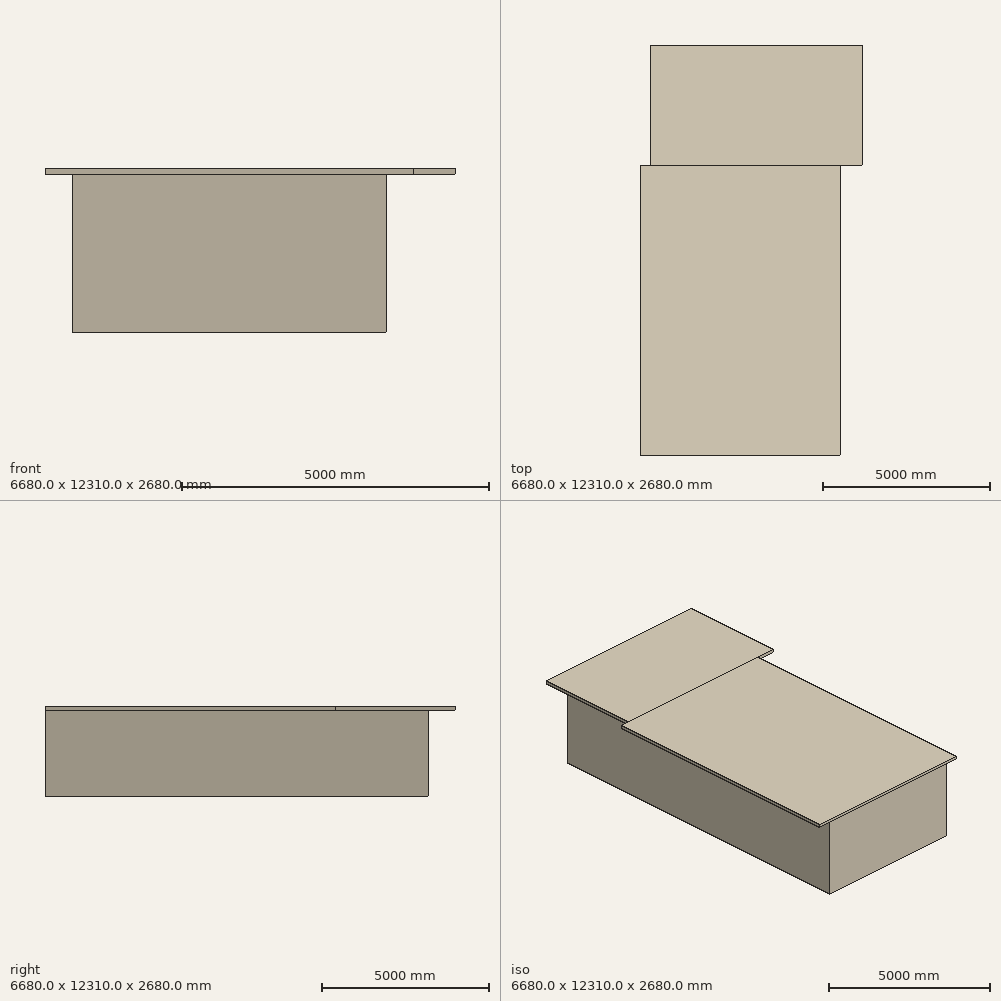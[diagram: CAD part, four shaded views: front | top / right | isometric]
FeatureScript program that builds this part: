
annotation { "Feature Type Name" : "Feature", "Feature Type Description" : "" }
export const myFeature = defineFeature(function(context is Context, id is Id, definition is map)
    precondition{}
    {
        {
            var Q0;
            Q0=qCreatedBy(makeId("Top.planeOp"),FACE);
            var sketch = newSketch(context, id + "F0", { "sketchPlane" : qUnion([Q0])});
            skLineSegment(sketch, "E0.bottom", {"start": v(0, 0) * mm, "end": v(5120, 0) * mm});
            skLineSegment(sketch, "E0.top", {"start": v(0, 11510) * mm, "end": v(5120, 11510) * mm});
            skLineSegment(sketch, "E0.left", {"start": v(0, 0) * mm, "end": v(0, 11510) * mm});
            skLineSegment(sketch, "E0.right", {"start": v(5120, 0) * mm, "end": v(5120, 11510) * mm});
            skLineSegment(sketch, "E1.bottom", {"start": v(5120, 11510) * mm, "end": v(0, 11510) * mm});
            skSolve(sketch);
        }
        {
            var Q0;
            Q0 = qSketchRegion(id + "F0", true);
            extrude(context, id + "F1", {"entities" : qUnion([Q0]), "depth" : 2580 * mm, "offsetDistance" : 25 * mm});
        }
        {
            var Q0;
            Q0=qCreatedBy(makeId("Front.planeOp"),FACE);
            var sketch = newSketch(context, id + "F2", { "sketchPlane" : qUnion([Q0])});
            skLineSegment(sketch, "E2.bottom", {"start": v(-440, 2580) * mm, "end": v(5560, 2580) * mm});
            skLineSegment(sketch, "E2.top", {"start": v(-440, 2680) * mm, "end": v(5560, 2680) * mm});
            skLineSegment(sketch, "E2.left", {"start": v(-440, 2580) * mm, "end": v(-440, 2680) * mm});
            skLineSegment(sketch, "E2.right", {"start": v(5560, 2580) * mm, "end": v(5560, 2680) * mm});
            skSolve(sketch);
        }
        {
            var Q0;
            Q0=makeQuery(id+"F2.imprint","IMPRINT",FACE,{"disambiguationData":[TD([[makeQuery(id+"F2.imprint","IMPRINT",EDGE,{"derivedFrom":sQuery(id+"F2.wireOp",EDGE,"E2.bottom")}),1.0]])]});
            extrude(context, id + "F3", {"entities" : qUnion([Q0]), "oppositeDirection" : true, "depth" : 8710 * mm, "offsetDistance" : 25 * mm});
        }
        {
            var Q0;
            Q0=makeQuery(id+"F3.opExtrude","SWEPT_FACE",FACE,{"disambiguationData":[OSD([sQuery(id+"F2.wireOp",EDGE,"E2.top")])]});
            var sketch = newSketch(context, id + "F4", { "sketchPlane" : qUnion([Q0])});
            skLineSegment(sketch, "E3.top", {"start": v(0, 8710) * mm, "end": v(5120, 8710) * mm});
            skLineSegment(sketch, "E4.bottom", {"start": v(6240, 8710) * mm, "end": v(-140, 8710) * mm});
            skLineSegment(sketch, "E4.top", {"start": v(6240, 12310) * mm, "end": v(-140, 12310) * mm});
            skLineSegment(sketch, "E4.left", {"start": v(6240, 8710) * mm, "end": v(6240, 12310) * mm});
            skLineSegment(sketch, "E4.right", {"start": v(-140, 8710) * mm, "end": v(-140, 12310) * mm});
            skSolve(sketch);
        }
        {
            var Q0;
            Q0 = qSketchRegion(id + "F4", true);
            extrude(context, id + "F5", {"entities" : qUnion([Q0]), "oppositeDirection" : true, "depth" : 100 * mm, "offsetDistance" : 25 * mm});
        }
    });
